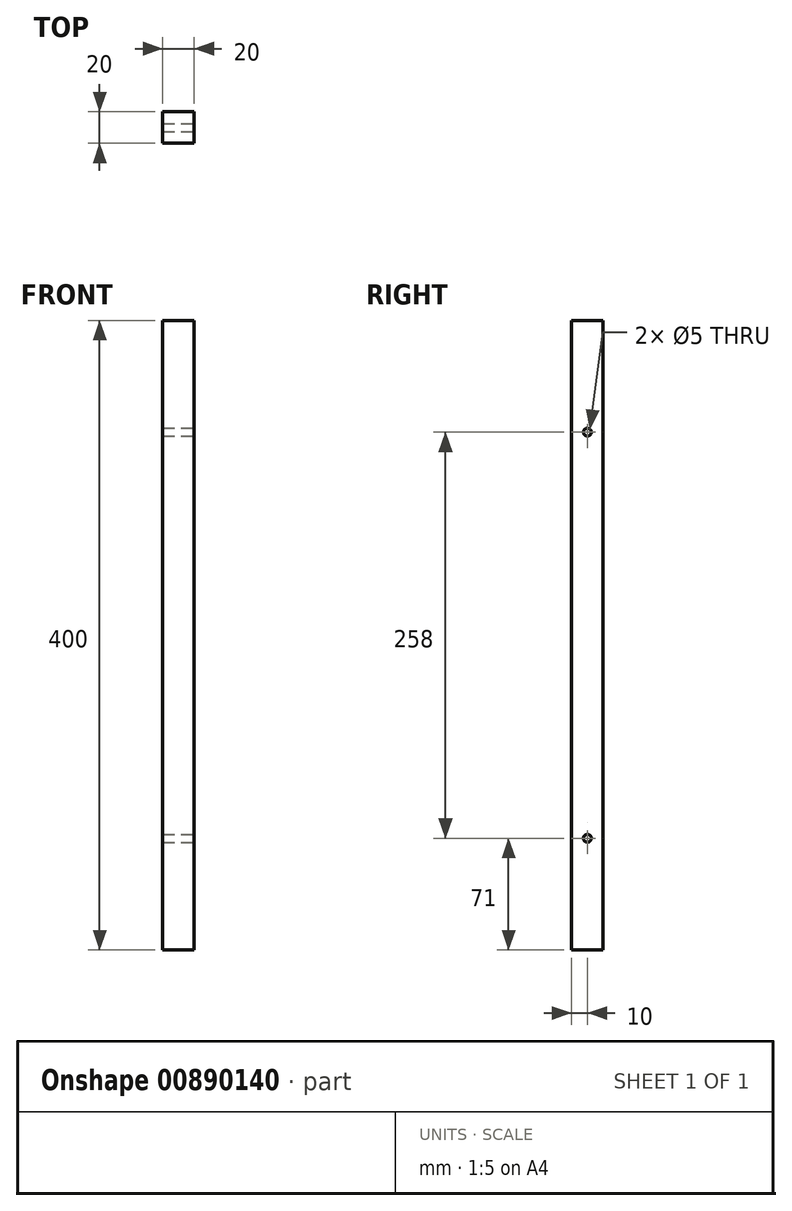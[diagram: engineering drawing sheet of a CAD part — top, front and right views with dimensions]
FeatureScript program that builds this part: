
annotation { "Feature Type Name" : "Feature", "Feature Type Description" : "" }
export const myFeature = defineFeature(function(context is Context, id is Id, definition is map)
    precondition{}
    {
        {
            var Q0;
            Q0=qCreatedBy(makeId("Front.planeOp"),FACE);
            var sketch = newSketch(context, id + "F0", { "sketchPlane" : qUnion([Q0])});
            skLineSegment(sketch, "E0", {"start": v(-10, 0) * mm, "end": v(10, 0) * mm});
            skLineSegment(sketch, "E1", {"start": v(10, 0) * mm, "end": v(10, 400) * mm});
            skLineSegment(sketch, "E2", {"start": v(10, 400) * mm, "end": v(-10, 400) * mm});
            skLineSegment(sketch, "E3", {"start": v(-10, 400) * mm, "end": v(-10, 0) * mm});
            skPoint(sketch, "E4.centerSnap0", {"position": v(0, 400) * mm});
            skSolve(sketch);
        }
        {
            var Q0;
            Q0=qSketchRegion(id+"F0",true);
            extrude(context, id + "F1", {"entities" : qUnion([Q0]), "depth" : 20 * mm, "offsetDistance" : 25 * mm});
        }
        {
            var Q0;
            Q0=makeQuery(id+"F1.opExtrude","SWEPT_FACE",FACE,{"disambiguationData":[OSD([sQuery(id+"F0.wireOp",EDGE,"E1")])]});
            var sketch = newSketch(context, id + "F2", { "sketchPlane" : qUnion([Q0])});
            skCircle(sketch, "E5", {"center": v(-10, 71) * mm, "radius": 2.5 * mm});
            skCircle(sketch, "E6", {"center": v(-10, 329) * mm, "radius": 2.5 * mm});
            skSolve(sketch);
        }
        {
            var Q0;
            Q0 = qSketchRegion(id + "F2", true);
            extrude(context, id + "F3", {"entities" : qUnion([Q0]), "operationType" : NewBodyOperationType.REMOVE, "oppositeDirection" : true, "depth" : 25 * mm, "offsetDistance" : 25 * mm});
        }
    });
